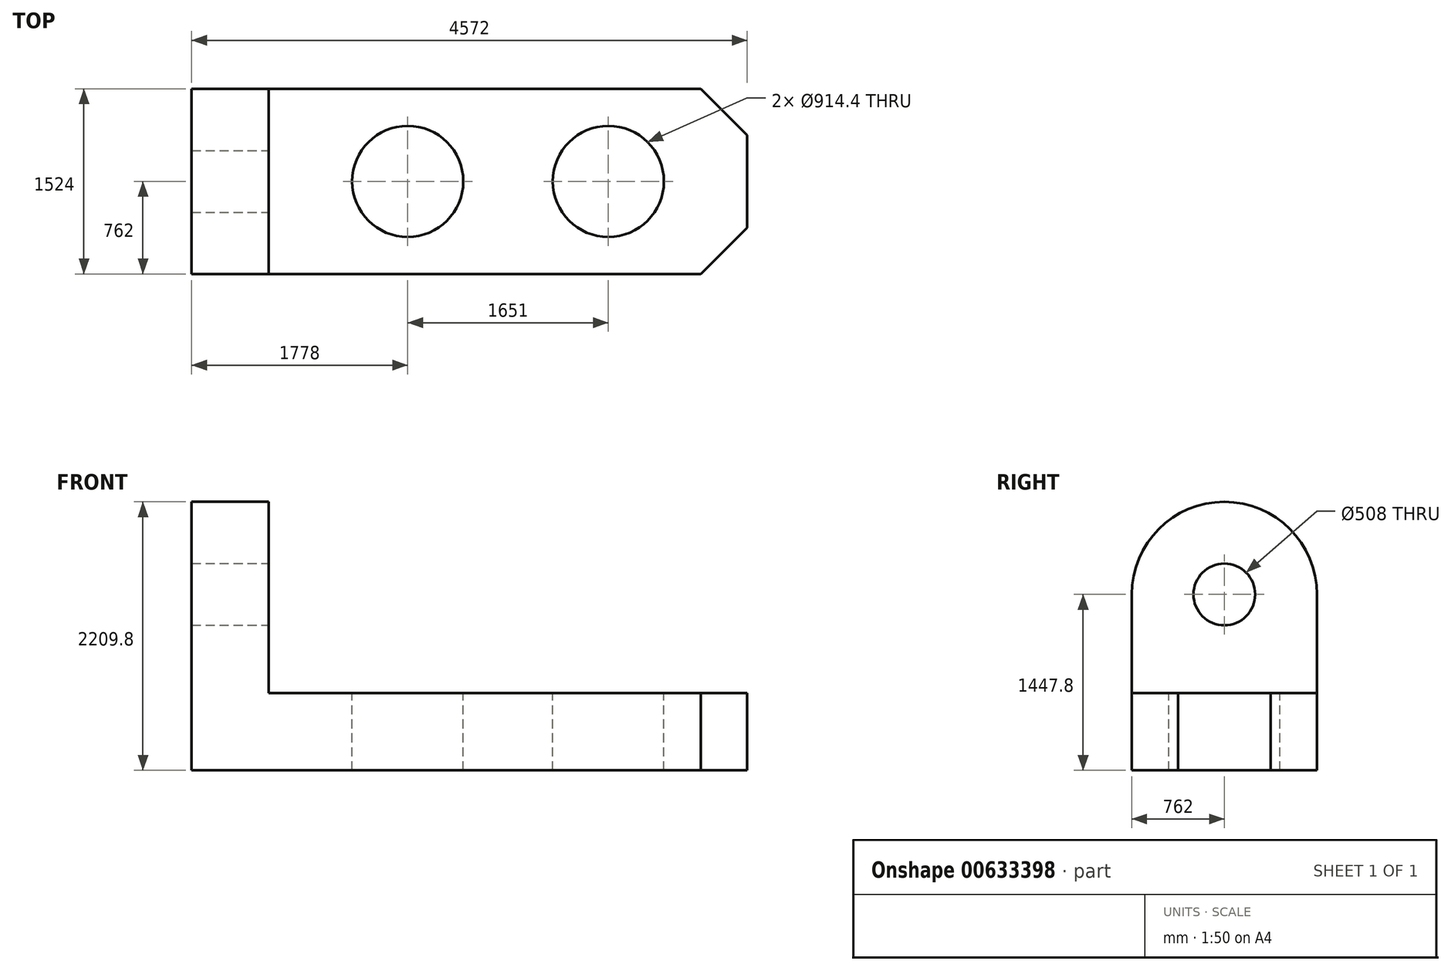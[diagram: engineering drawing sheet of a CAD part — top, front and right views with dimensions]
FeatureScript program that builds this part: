
annotation { "Feature Type Name" : "Feature", "Feature Type Description" : "" }
export const myFeature = defineFeature(function(context is Context, id is Id, definition is map)
    precondition{}
    {
        {
            var Q0;
            Q0=qCreatedBy(makeId("Top.planeOp"),FACE);
            var sketch = newSketch(context, id + "F0", { "sketchPlane" : qUnion([Q0])});
            skLineSegment(sketch, "E0.bottom", {"start": v(0, 0) * mm, "end": v(4572, 0) * mm});
            skLineSegment(sketch, "E0.top", {"start": v(0, 1524) * mm, "end": v(4572, 1524) * mm});
            skLineSegment(sketch, "E0.left", {"start": v(0, 0) * mm, "end": v(0, 1524) * mm});
            skLineSegment(sketch, "E0.right", {"start": v(4572, 0) * mm, "end": v(4572, 1524) * mm});
            skSolve(sketch);
        }
        {
            var Q0;
            Q0=makeQuery(id+"F0.imprint","IMPRINT",FACE,{"disambiguationData":[TD([[makeQuery(id+"F0.imprint","IMPRINT",EDGE,{"derivedFrom":sQuery(id+"F0.wireOp",EDGE,"E0.bottom")}),1.0]])]});
            extrude(context, id + "F1", {"entities" : qUnion([Q0]), "depth" : 635 * mm, "offsetDistance" : 25.4 * mm});
        }
        {
            var Q0;
            Q0=makeQuery(id+"F1.opExtrude","CAP_FACE",FACE,{"disambiguationData":[OSD([sQuery(id+"F0.wireOp",EDGE,"E0.bottom"),sQuery(id+"F0.wireOp",EDGE,"E0.top"),sQuery(id+"F0.wireOp",EDGE,"E0.left"),sQuery(id+"F0.wireOp",EDGE,"E0.right")])],"isStart":false});
            var sketch = newSketch(context, id + "F2", { "sketchPlane" : qUnion([Q0])});
            skLineSegment(sketch, "E1.bottom", {"start": v(0, 0) * mm, "end": v(635, 0) * mm});
            skLineSegment(sketch, "E1.top", {"start": v(0, 1524) * mm, "end": v(635, 1524) * mm});
            skLineSegment(sketch, "E1.left", {"start": v(0, 0) * mm, "end": v(0, 1524) * mm});
            skLineSegment(sketch, "E1.right", {"start": v(635, 0) * mm, "end": v(635, 1524) * mm});
            skSolve(sketch);
        }
        {
            var Q0;
            Q0=makeQuery(id+"F2.imprint","IMPRINT",FACE,{"disambiguationData":[TD([[makeQuery(id+"F2.imprint","IMPRINT",EDGE,{"derivedFrom":sQuery(id+"F2.wireOp",EDGE,"E1.bottom")}),1.0]])]});
            extrude(context, id + "F3", {"entities" : qUnion([Q0]), "operationType" : NewBodyOperationType.ADD, "depth" : 1574.8 * mm, "offsetDistance" : 25.4 * mm});
        }
        {
            var Q0;
            Q0=makeQuery(id+"F3.opExtrude","CAP_EDGE",EDGE,{"disambiguationData":[OSD([sQuery(id+"F2.wireOp",EDGE,"E1.bottom")])],"isStart":false});
            fillet(context, id + "F4", {"entities" : qUnion([Q0]), "radius" : 762 * mm, "tangentPropagation" : true, "allowEdgeOverflow" : false});
        }
        {
            var Q0;
            Q0=makeQuery(id+"F3.opExtrude","CAP_EDGE",EDGE,{"disambiguationData":[OSD([sQuery(id+"F2.wireOp",EDGE,"E1.top")])],"isStart":false});
            fillet(context, id + "F5", {"entities" : qUnion([Q0]), "radius" : 762 * mm, "tangentPropagation" : true, "allowEdgeOverflow" : false});
        }
        {
            var Q0;
            Q0=makeQuery(id+"F1.opExtrude","CAP_FACE",FACE,{"disambiguationData":[OSD([sQuery(id+"F0.wireOp",EDGE,"E0.bottom"),sQuery(id+"F0.wireOp",EDGE,"E0.top"),sQuery(id+"F0.wireOp",EDGE,"E0.left"),sQuery(id+"F0.wireOp",EDGE,"E0.right")])],"isStart":false});
            var sketch = newSketch(context, id + "F6", { "sketchPlane" : qUnion([Q0])});
            skCircle(sketch, "E2", {"center": v(1778, 762) * mm, "radius": 457.2 * mm});
            skCircle(sketch, "E3", {"center": v(3429, 762) * mm, "radius": 457.2 * mm});
            skSolve(sketch);
        }
        {
            var Q0;
            Q0=makeQuery(id+"F6.imprint","IMPRINT",FACE,{"disambiguationData":[TD([[makeQuery(id+"F6.imprint","IMPRINT",EDGE,{"derivedFrom":sQuery(id+"F6.wireOp",EDGE,"E2")}),1.0]])]});
            var Q1;
            Q1=makeQuery(id+"F6.imprint","IMPRINT",FACE,{"disambiguationData":[TD([[makeQuery(id+"F6.imprint","IMPRINT",EDGE,{"derivedFrom":sQuery(id+"F6.wireOp",EDGE,"E3")}),1.0]])]});
            extrude(context, id + "F7", {"entities" : qUnion([Q0, Q1]), "operationType" : NewBodyOperationType.REMOVE, "endBound" : BoundingType.UP_TO_NEXT, "oppositeDirection" : true, "depth" : 25.4 * mm, "offsetDistance" : 25.4 * mm});
        }
        {
            var Q0;
            Q0=makeQuery(id+"F3.opExtrude","SWEPT_FACE",FACE,{"disambiguationData":[OSD([sQuery(id+"F2.wireOp",EDGE,"E1.right")])]});
            var sketch = newSketch(context, id + "F8", { "sketchPlane" : qUnion([Q0])});
            skCircle(sketch, "E4", {"center": v(762, 1447.8) * mm, "radius": 254 * mm});
            skSolve(sketch);
        }
        {
            var Q0;
            Q0=makeQuery(id+"F8.imprint","IMPRINT",FACE,{"disambiguationData":[TD([[makeQuery(id+"F8.imprint","IMPRINT",EDGE,{"derivedFrom":sQuery(id+"F8.wireOp",EDGE,"E4")}),1.0]])]});
            extrude(context, id + "F9", {"entities" : qUnion([Q0]), "operationType" : NewBodyOperationType.REMOVE, "endBound" : BoundingType.UP_TO_NEXT, "oppositeDirection" : true, "depth" : 25.4 * mm, "offsetDistance" : 25.4 * mm});
        }
        {
            var Q0;
            Q0=makeQuery(id+"F1.opExtrude","SWEPT_EDGE",EDGE,{"disambiguationData":[OSD([sQuery(id+"F0.wireOp",EDGE,"E0.bottom"),sQuery(id+"F0.wireOp",EDGE,"E0.right")])]});
            chamfer(context, id + "F10", {"entities" : qUnion([Q0]), "width" : 381 * mm, "tangentPropagation" : true});
        }
        {
            var Q0;
            Q0=makeQuery(id+"F1.opExtrude","SWEPT_EDGE",EDGE,{"disambiguationData":[OSD([sQuery(id+"F0.wireOp",EDGE,"E0.top"),sQuery(id+"F0.wireOp",EDGE,"E0.right")])]});
            chamfer(context, id + "F11", {"entities" : qUnion([Q0]), "width" : 381 * mm, "tangentPropagation" : true});
        }
    });
